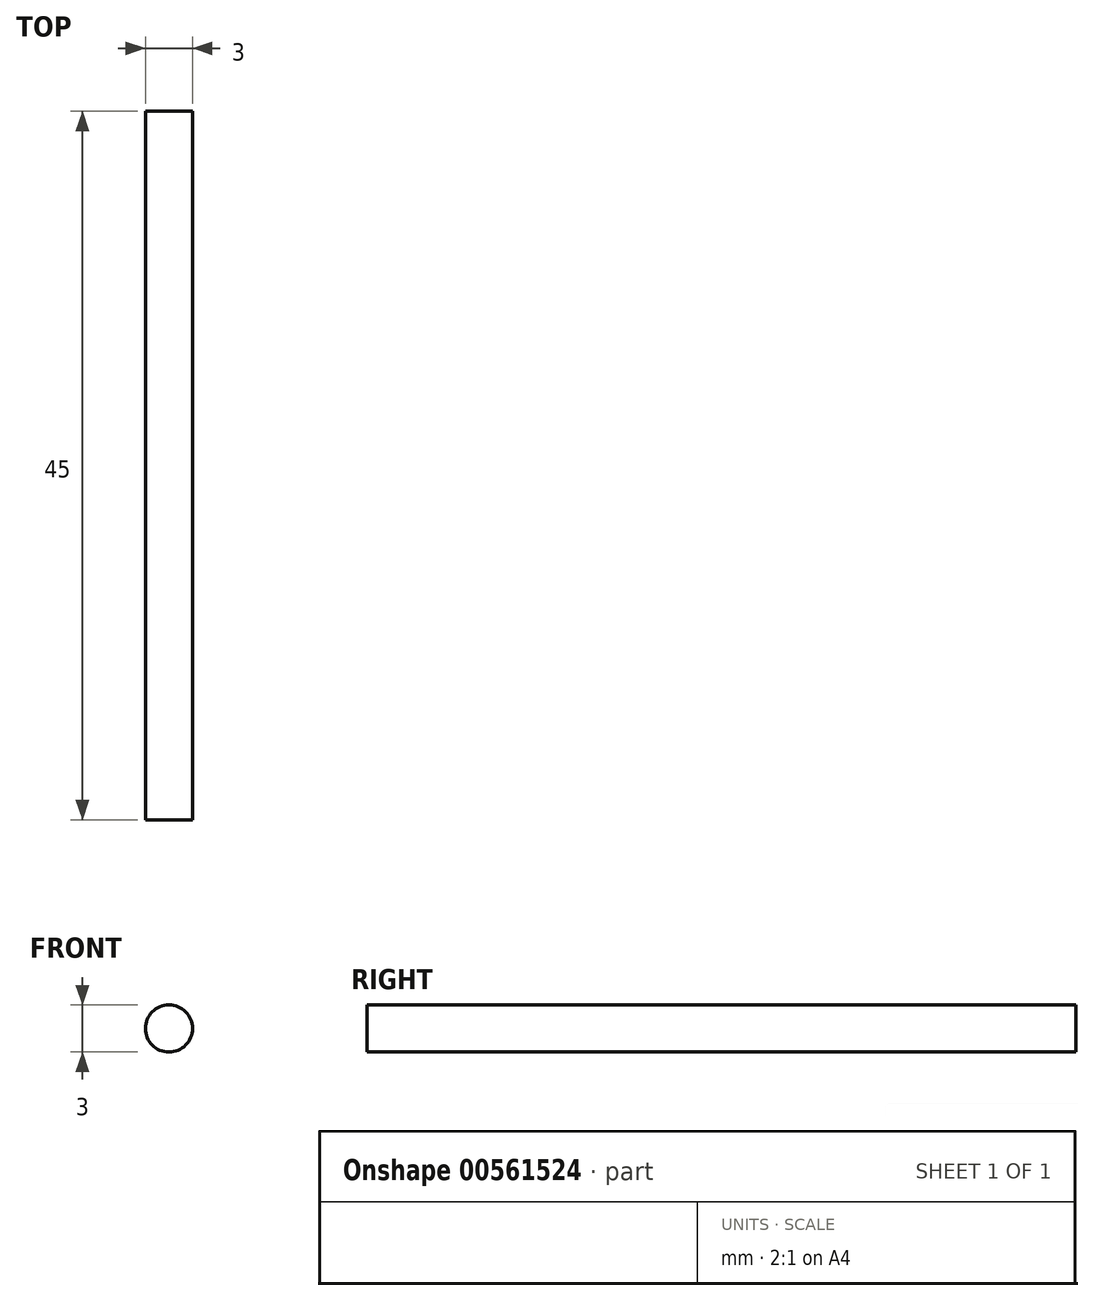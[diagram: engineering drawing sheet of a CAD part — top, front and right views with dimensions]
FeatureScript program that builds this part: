
annotation { "Feature Type Name" : "Feature", "Feature Type Description" : "" }
export const myFeature = defineFeature(function(context is Context, id is Id, definition is map)
    precondition{}
    {
        {
            var Q0;
            Q0=qCreatedBy(makeId("Front.planeOp"),FACE);
            var sketch = newSketch(context, id + "F0", { "sketchPlane" : qUnion([Q0])});
            skCircle(sketch, "E0", {"center": v(0, 0) * mm, "radius": 1.5 * mm});
            skSolve(sketch);
        }
        {
            var Q0;
            Q0=makeQuery(id+"F0.imprint","IMPRINT",FACE,{"disambiguationData":[TD([[makeQuery(id+"F0.imprint","IMPRINT",EDGE,{"derivedFrom":sQuery(id+"F0.wireOp",EDGE,"E0")}),1.0]])]});
            extrude(context, id + "F1", {"entities" : qUnion([Q0]), "depth" : 45 * mm, "offsetDistance" : 25 * mm});
        }
    });
